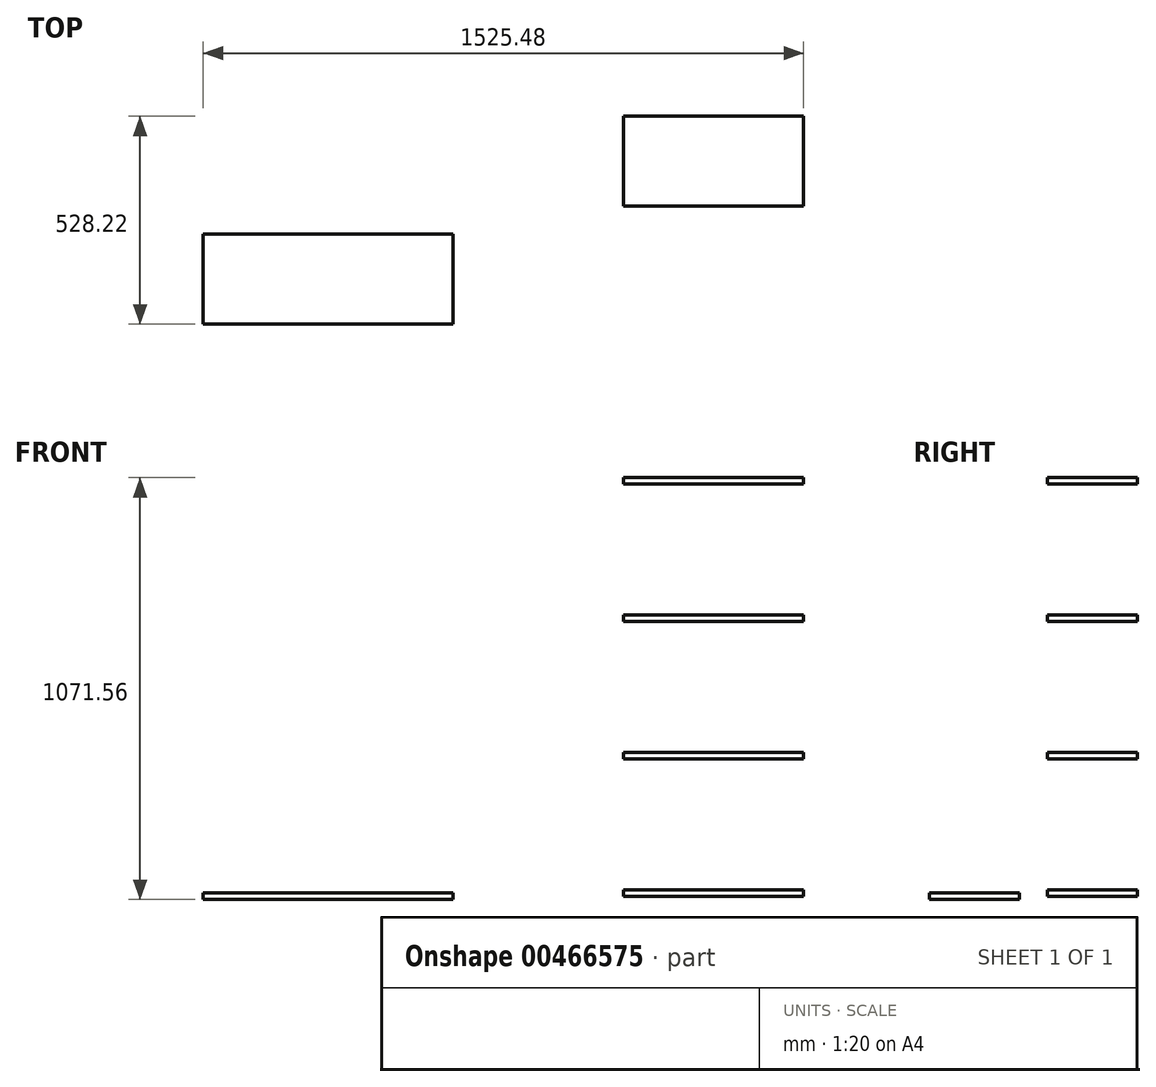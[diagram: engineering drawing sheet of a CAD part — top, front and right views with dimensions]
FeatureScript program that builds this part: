
annotation { "Feature Type Name" : "Feature", "Feature Type Description" : "" }
export const myFeature = defineFeature(function(context is Context, id is Id, definition is map)
    precondition{}
    {
        {
            var Q0;
            Q0=qCreatedBy(makeId("Top.planeOp"),FACE);
            var sketch = newSketch(context, id + "F0", { "sketchPlane" : qUnion([Q0])});
            skLineSegment(sketch, "E0.bottom", {"start": v(-317.5, -114.3) * mm, "end": v(317.5, -114.3) * mm});
            skLineSegment(sketch, "E0.top", {"start": v(-317.5, 114.3) * mm, "end": v(317.5, 114.3) * mm});
            skLineSegment(sketch, "E0.left", {"start": v(-317.5, -114.3) * mm, "end": v(-317.5, 114.3) * mm});
            skLineSegment(sketch, "E0.right", {"start": v(317.5, -114.3) * mm, "end": v(317.5, 114.3) * mm});
            skPoint(sketch, "E0.middle", {"position": v(0, 0) * mm});
            skSolve(sketch);
        }
        {
            var Q0;
            Q0 = qSketchRegion(id + "F0", true);
            extrude(context, id + "F1", {"entities" : qUnion([Q0]), "endBound" : BoundingType.SYMMETRIC, "depth" : 15.88 * mm});
        }
        {
            var Q0;
            Q0=qCreatedBy(makeId("Top.planeOp"),FACE);
            var sketch = newSketch(context, id + "F2", { "sketchPlane" : qUnion([Q0])});
            skLineSegment(sketch, "E1.bottom", {"start": v(750.78, 185.32) * mm, "end": v(1207.98, 185.32) * mm});
            skLineSegment(sketch, "E1.top", {"start": v(750.78, 413.92) * mm, "end": v(1207.98, 413.92) * mm});
            skLineSegment(sketch, "E1.left", {"start": v(750.78, 185.32) * mm, "end": v(750.78, 413.92) * mm});
            skLineSegment(sketch, "E1.right", {"start": v(1207.98, 185.32) * mm, "end": v(1207.98, 413.92) * mm});
            skPoint(sketch, "E1.middle", {"position": v(979.38, 299.62) * mm});
            skSolve(sketch);
        }
        {
            var Q0;
            Q0 = qSketchRegion(id + "F2", true);
            extrude(context, id + "F3", {"entities" : qUnion([Q0]), "depth" : 15.88 * mm});
        }
        {
            var Q0;
            Q0=makeQuery(id+"F3.opExtrude","SWEPT_BODY",BODY,{"disambiguationData":[OSD([sQuery(id+"F2.wireOp",EDGE,"E1.bottom"),sQuery(id+"F2.wireOp",EDGE,"E1.top"),sQuery(id+"F2.wireOp",EDGE,"E1.left"),sQuery(id+"F2.wireOp",EDGE,"E1.right")])]});
            transform(context, id + "F4", {"entities" : qUnion([Q0]), "transformType" : TransformType.TRANSLATION_3D, "dx" : 0 * mm, "dy" : 0 * mm, "dz" : 349.25 * mm, "makeCopy" : true});
        }
        {
            var Q0;
            Q0=makeQuery(id+"F4.opPattern","COPY",BODY,{"derivedFrom":makeQuery(id+"F3.opExtrude","SWEPT_BODY",BODY,{"disambiguationData":[OSD([sQuery(id+"F2.wireOp",EDGE,"E1.bottom"),sQuery(id+"F2.wireOp",EDGE,"E1.top"),sQuery(id+"F2.wireOp",EDGE,"E1.left"),sQuery(id+"F2.wireOp",EDGE,"E1.right")])]}),"instanceName":"1"});
            transform(context, id + "F5", {"entities" : qUnion([Q0]), "transformType" : TransformType.TRANSLATION_3D, "dx" : 0 * mm, "dy" : 0 * mm, "dz" : 349.25 * mm, "makeCopy" : true});
        }
        {
            var Q0;
            Q0=makeQuery(id+"F5.opPattern","COPY",BODY,{"derivedFrom":makeQuery(id+"F4.opPattern","COPY",BODY,{"derivedFrom":makeQuery(id+"F3.opExtrude","SWEPT_BODY",BODY,{"disambiguationData":[OSD([sQuery(id+"F2.wireOp",EDGE,"E1.bottom"),sQuery(id+"F2.wireOp",EDGE,"E1.top"),sQuery(id+"F2.wireOp",EDGE,"E1.left"),sQuery(id+"F2.wireOp",EDGE,"E1.right")])]}),"instanceName":"1"}),"instanceName":"1"});
            transform(context, id + "F6", {"entities" : qUnion([Q0]), "transformType" : TransformType.TRANSLATION_3D, "dx" : 0 * mm, "dy" : 0 * mm, "dz" : 349.25 * mm, "makeCopy" : true});
        }
    });
